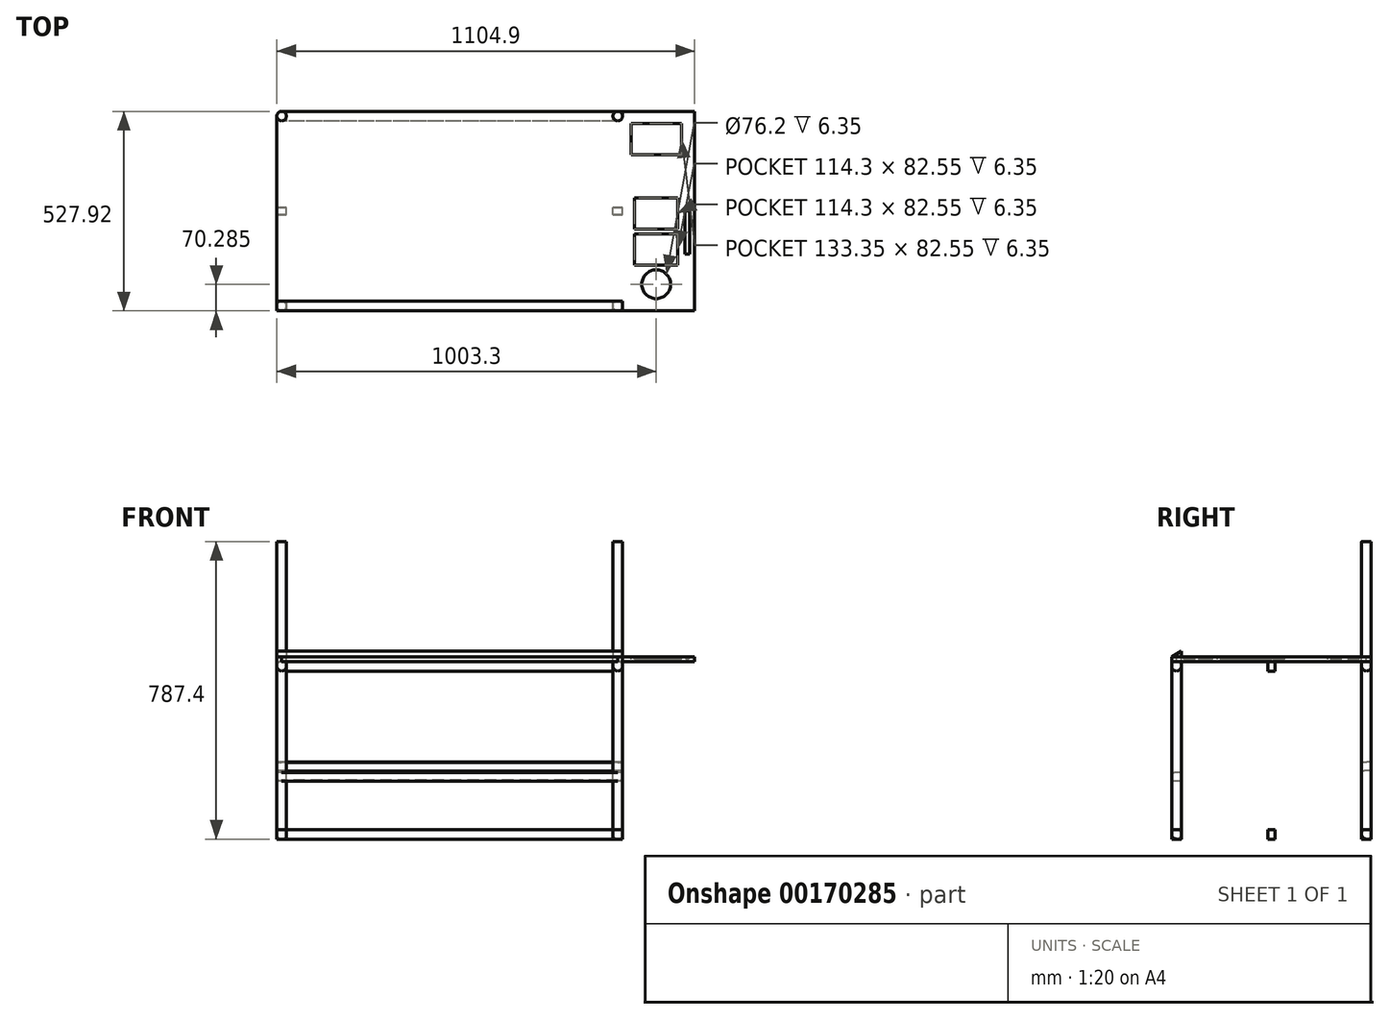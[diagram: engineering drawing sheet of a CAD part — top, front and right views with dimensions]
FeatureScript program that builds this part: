
annotation { "Feature Type Name" : "Feature", "Feature Type Description" : "" }
export const myFeature = defineFeature(function(context is Context, id is Id, definition is map)
    precondition{}
    {
        {
            var Q0;
            Q0=qCreatedBy(makeId("Top.planeOp"),FACE);
            var sketch = newSketch(context, id + "F0", { "sketchPlane" : qUnion([Q0])});
            skLineSegment(sketch, "E0.bottom", {"start": v(444.5, 251.26) * mm, "end": v(-444.5, 251.26) * mm});
            skLineSegment(sketch, "E0.top", {"start": v(444.5, -251.26) * mm, "end": v(-444.5, -251.26) * mm});
            skLineSegment(sketch, "E0.left", {"start": v(444.5, 251.26) * mm, "end": v(444.5, -251.26) * mm});
            skLineSegment(sketch, "E0.right", {"start": v(-444.5, 251.26) * mm, "end": v(-444.5, -251.26) * mm});
            skPoint(sketch, "E0.middle", {"position": v(0, 0) * mm});
            skCircle(sketch, "E1", {"center": v(-444.5, 251.26) * mm, "radius": 12.7 * mm});
            skCircle(sketch, "E2", {"center": v(-444.5, -251.26) * mm, "radius": 12.7 * mm});
            skCircle(sketch, "E3", {"center": v(444.5, -251.26) * mm, "radius": 12.7 * mm});
            skCircle(sketch, "E4", {"center": v(444.5, 251.26) * mm, "radius": 12.7 * mm});
            skLineSegment(sketch, "E5.bottom", {"start": v(-457.2, 263.96) * mm, "end": v(457.2, 263.96) * mm});
            skLineSegment(sketch, "E5.top", {"start": v(-457.2, -263.96) * mm, "end": v(457.2, -263.96) * mm});
            skLineSegment(sketch, "E5.left", {"start": v(-457.2, 263.96) * mm, "end": v(-457.2, -263.96) * mm});
            skLineSegment(sketch, "E5.right", {"start": v(457.2, 263.96) * mm, "end": v(457.2, -263.96) * mm});
            skLineSegment(sketch, "E6", {"start": v(457.2, 0) * mm, "end": v(647.7, 0) * mm});
            skPoint(sketch, "E6.endSnap0", {"position": v(457.2, 0) * mm});
            skLineSegment(sketch, "E7", {"start": v(647.7, 0) * mm, "end": v(647.7, 263.96) * mm});
            skLineSegment(sketch, "E8.bottom", {"start": v(647.7, 263.96) * mm, "end": v(457.2, 263.96) * mm});
            skLineSegment(sketch, "E8.top", {"start": v(647.7, -263.96) * mm, "end": v(457.2, -263.96) * mm});
            skPoint(sketch, "E9.centerSnap0", {"position": v(647.7, 131.98) * mm});
            skPoint(sketch, "E9.centerSnap1", {"position": v(552.45, 263.96) * mm});
            skLineSegment(sketch, "E10", {"start": v(647.7, 0) * mm, "end": v(647.7, -263.96) * mm});
            skSolve(sketch);
        }
        {
            var Q0;
            {var subQ0=sQuery(id+"F0.wireOp",EDGE,"E0.right");var subQ1=sQuery(id+"F0.wireOp",EDGE,"E0.bottom");var subQ2=makeQuery(id+"F0.imprint","INTERSECT",VERTEX,{"derivedFrom":[subQ1,subQ0]});Q0=makeQuery(id+"F0.imprint","IMPRINT",FACE,{"disambiguationData":[TD([[makeQuery(id+"F0.imprint","IMPRINT",EDGE,{"disambiguationData":[TD([[subQ2,1.0]])],"derivedFrom":subQ1}),-1.0]])]});}
            var Q1;
            {var subQ0=sQuery(id+"F0.wireOp",EDGE,"E0.right");var subQ1=sQuery(id+"F0.wireOp",EDGE,"E0.bottom");var subQ2=makeQuery(id+"F0.imprint","INTERSECT",VERTEX,{"derivedFrom":[subQ1,subQ0]});Q1=makeQuery(id+"F0.imprint","IMPRINT",FACE,{"disambiguationData":[TD([[makeQuery(id+"F0.imprint","IMPRINT",EDGE,{"disambiguationData":[TD([[subQ2,1.0]])],"derivedFrom":subQ1}),1.0]])]});}
            var Q2;
            {var subQ0=sQuery(id+"F0.wireOp",EDGE,"E0.left");var subQ1=sQuery(id+"F0.wireOp",EDGE,"E0.bottom");var subQ2=makeQuery(id+"F0.imprint","INTERSECT",VERTEX,{"derivedFrom":[subQ1,subQ0]});Q2=makeQuery(id+"F0.imprint","IMPRINT",FACE,{"disambiguationData":[TD([[makeQuery(id+"F0.imprint","IMPRINT",EDGE,{"disambiguationData":[TD([[subQ2,-1.0]])],"derivedFrom":subQ1}),-1.0]])]});}
            var Q3;
            {var subQ0=sQuery(id+"F0.wireOp",EDGE,"E0.left");var subQ1=sQuery(id+"F0.wireOp",EDGE,"E0.bottom");var subQ2=makeQuery(id+"F0.imprint","INTERSECT",VERTEX,{"derivedFrom":[subQ1,subQ0]});Q3=makeQuery(id+"F0.imprint","IMPRINT",FACE,{"disambiguationData":[TD([[makeQuery(id+"F0.imprint","IMPRINT",EDGE,{"disambiguationData":[TD([[subQ2,-1.0]])],"derivedFrom":subQ1}),1.0]])]});}
            extrude(context, id + "F1", {"entities" : qUnion([Q0, Q1, Q2, Q3]), "depth" : 304.8 * mm});
        }
        {
            var Q0;
            {var subQ0=sQuery(id+"F0.wireOp",EDGE,"E0.right");var subQ1=sQuery(id+"F0.wireOp",EDGE,"E0.top");var subQ2=makeQuery(id+"F0.imprint","INTERSECT",VERTEX,{"derivedFrom":[subQ1,subQ0]});Q0=makeQuery(id+"F0.imprint","IMPRINT",FACE,{"disambiguationData":[TD([[makeQuery(id+"F0.imprint","IMPRINT",EDGE,{"disambiguationData":[TD([[subQ2,1.0]])],"derivedFrom":subQ1}),1.0]])]});}
            var Q1;
            {var subQ0=sQuery(id+"F0.wireOp",EDGE,"E0.right");var subQ1=sQuery(id+"F0.wireOp",EDGE,"E0.top");var subQ2=makeQuery(id+"F0.imprint","INTERSECT",VERTEX,{"derivedFrom":[subQ1,subQ0]});Q1=makeQuery(id+"F0.imprint","IMPRINT",FACE,{"disambiguationData":[TD([[makeQuery(id+"F0.imprint","IMPRINT",EDGE,{"disambiguationData":[TD([[subQ2,1.0]])],"derivedFrom":subQ1}),-1.0]])]});}
            var Q2;
            {var subQ0=sQuery(id+"F0.wireOp",EDGE,"E0.left");var subQ1=sQuery(id+"F0.wireOp",EDGE,"E0.top");var subQ2=makeQuery(id+"F0.imprint","INTERSECT",VERTEX,{"derivedFrom":[subQ1,subQ0]});Q2=makeQuery(id+"F0.imprint","IMPRINT",FACE,{"disambiguationData":[TD([[makeQuery(id+"F0.imprint","IMPRINT",EDGE,{"disambiguationData":[TD([[subQ2,-1.0]])],"derivedFrom":subQ1}),-1.0]])]});}
            var Q3;
            {var subQ0=sQuery(id+"F0.wireOp",EDGE,"E0.left");var subQ1=sQuery(id+"F0.wireOp",EDGE,"E0.top");var subQ2=makeQuery(id+"F0.imprint","INTERSECT",VERTEX,{"derivedFrom":[subQ1,subQ0]});Q3=makeQuery(id+"F0.imprint","IMPRINT",FACE,{"disambiguationData":[TD([[makeQuery(id+"F0.imprint","IMPRINT",EDGE,{"disambiguationData":[TD([[subQ2,-1.0]])],"derivedFrom":subQ1}),1.0]])]});}
            extrude(context, id + "F2", {"entities" : qUnion([Q0, Q1, Q2, Q3]), "oppositeDirection" : true, "depth" : 457.2 * mm});
        }
        {
            var Q0;
            {var subQ0=sQuery(id+"F0.wireOp",EDGE,"E0.left");var subQ1=sQuery(id+"F0.wireOp",EDGE,"E0.bottom");var subQ2=makeQuery(id+"F0.imprint","INTERSECT",VERTEX,{"derivedFrom":[subQ1,subQ0]});Q0=makeQuery(id+"F0.imprint","IMPRINT",FACE,{"disambiguationData":[TD([[makeQuery(id+"F0.imprint","IMPRINT",EDGE,{"disambiguationData":[TD([[subQ2,-1.0]])],"derivedFrom":subQ1}),1.0]])]});}
            var Q1;
            {var subQ0=sQuery(id+"F0.wireOp",EDGE,"E0.left");var subQ1=sQuery(id+"F0.wireOp",EDGE,"E0.bottom");var subQ2=makeQuery(id+"F0.imprint","INTERSECT",VERTEX,{"derivedFrom":[subQ1,subQ0]});Q1=makeQuery(id+"F0.imprint","IMPRINT",FACE,{"disambiguationData":[TD([[makeQuery(id+"F0.imprint","IMPRINT",EDGE,{"disambiguationData":[TD([[subQ2,-1.0]])],"derivedFrom":subQ1}),-1.0]])]});}
            var Q2;
            {var subQ0=sQuery(id+"F0.wireOp",EDGE,"E0.right");var subQ1=sQuery(id+"F0.wireOp",EDGE,"E0.bottom");var subQ2=makeQuery(id+"F0.imprint","INTERSECT",VERTEX,{"derivedFrom":[subQ1,subQ0]});Q2=makeQuery(id+"F0.imprint","IMPRINT",FACE,{"disambiguationData":[TD([[makeQuery(id+"F0.imprint","IMPRINT",EDGE,{"disambiguationData":[TD([[subQ2,1.0]])],"derivedFrom":subQ1}),1.0]])]});}
            var Q3;
            {var subQ0=sQuery(id+"F0.wireOp",EDGE,"E0.right");var subQ1=sQuery(id+"F0.wireOp",EDGE,"E0.bottom");var subQ2=makeQuery(id+"F0.imprint","INTERSECT",VERTEX,{"derivedFrom":[subQ1,subQ0]});Q3=makeQuery(id+"F0.imprint","IMPRINT",FACE,{"disambiguationData":[TD([[makeQuery(id+"F0.imprint","IMPRINT",EDGE,{"disambiguationData":[TD([[subQ2,1.0]])],"derivedFrom":subQ1}),-1.0]])]});}
            extrude(context, id + "F3", {"entities" : qUnion([Q0, Q1, Q2, Q3]), "oppositeDirection" : true, "depth" : 457.2 * mm});
        }
        {
            var Q0;
            {var subQ0=sQuery(id+"F0.wireOp",EDGE,"E1");var subQ1=sQuery(id+"F0.wireOp",EDGE,"E0.right");var subQ2=makeQuery(id+"F0.imprint","INTERSECT",VERTEX,{"derivedFrom":[subQ1,subQ0]});Q0=makeQuery(id+"F0.imprint","IMPRINT",FACE,{"disambiguationData":[TD([[makeQuery(id+"F0.imprint","IMPRINT",EDGE,{"disambiguationData":[TD([[subQ2,-1.0]])],"derivedFrom":subQ1}),-1.0]])]});}
            var Q1;
            {var subQ0=sQuery(id+"F0.wireOp",EDGE,"E3");var subQ1=sQuery(id+"F0.wireOp",EDGE,"E0.top");var subQ2=makeQuery(id+"F0.imprint","INTERSECT",VERTEX,{"derivedFrom":[subQ1,subQ0]});Q1=makeQuery(id+"F0.imprint","IMPRINT",FACE,{"disambiguationData":[TD([[makeQuery(id+"F0.imprint","IMPRINT",EDGE,{"disambiguationData":[TD([[subQ2,-1.0]])],"derivedFrom":subQ1}),1.0]])]});}
            var Q2;
            {var subQ0=sQuery(id+"F0.wireOp",EDGE,"E4");var subQ1=sQuery(id+"F0.wireOp",EDGE,"E0.left");var subQ2=makeQuery(id+"F0.imprint","INTERSECT",VERTEX,{"derivedFrom":[subQ1,subQ0]});Q2=makeQuery(id+"F0.imprint","IMPRINT",FACE,{"disambiguationData":[TD([[makeQuery(id+"F0.imprint","IMPRINT",EDGE,{"disambiguationData":[TD([[subQ2,-1.0]])],"derivedFrom":subQ1}),1.0]])]});}
            var Q3;
            {var subQ0=sQuery(id+"F0.wireOp",EDGE,"E4");var subQ1=sQuery(id+"F0.wireOp",EDGE,"E0.bottom");var subQ2=makeQuery(id+"F0.imprint","INTERSECT",VERTEX,{"derivedFrom":[subQ1,subQ0]});Q3=makeQuery(id+"F0.imprint","IMPRINT",FACE,{"disambiguationData":[TD([[makeQuery(id+"F0.imprint","IMPRINT",EDGE,{"disambiguationData":[TD([[subQ2,-1.0]])],"derivedFrom":subQ1}),-1.0]])]});}
            var Q4;
            {var subQ5=sQuery(id+"F0.wireOp",EDGE,"E4");var subQ13=sQuery(id+"F0.wireOp",EDGE,"E0.bottom");var subQ14=makeQuery(id+"F0.imprint","INTERSECT",VERTEX,{"derivedFrom":[subQ13,subQ5]});Q4=makeQuery(id+"F0.imprint","IMPRINT",FACE,{"disambiguationData":[TD([[makeQuery(id+"F0.imprint","IMPRINT",EDGE,{"disambiguationData":[TD([[subQ14,-1.0]])],"derivedFrom":subQ13}),1.0]])]});}
            var Q5;
            {var subQ0=sQuery(id+"F0.wireOp",EDGE,"E6");Q5=makeQuery(id+"F0.imprint","IMPRINT",FACE,{"disambiguationData":[TD([[makeQuery(id+"F0.imprint","IMPRINT",EDGE,{"derivedFrom":subQ0}),1.0]])]});}
            var Q6;
            {var subQ0=sQuery(id+"F0.wireOp",EDGE,"E6");Q6=makeQuery(id+"F0.imprint","IMPRINT",FACE,{"disambiguationData":[TD([[makeQuery(id+"F0.imprint","IMPRINT",EDGE,{"derivedFrom":subQ0}),-1.0]])]});}
            extrude(context, id + "F4", {"entities" : qUnion([Q0, Q1, Q2, Q3, Q4, Q5, Q6]), "oppositeDirection" : true, "depth" : 12.7 * mm});
        }
        {
            var Q0;
            Q0=qCreatedBy(makeId("Top.planeOp"),FACE);
            cPlane(context, id + "F5", {"entities" : qUnion([Q0]), "cplaneType" : CPlaneType.OFFSET, "offset" : 457.2 * mm, "oppositeDirection" : true, "width" : 152.4 * mm, "height" : 152.4 * mm});
        }
        {
            var Q0;
            Q0=qCreatedBy(id+"F5.planeOp",FACE);
            var sketch = newSketch(context, id + "F6", { "sketchPlane" : qUnion([Q0])});
            skLineSegment(sketch, "E11.bottom", {"start": v(-457.2, 263.96) * mm, "end": v(457.2, 263.96) * mm});
            skLineSegment(sketch, "E11.top", {"start": v(-457.2, -263.96) * mm, "end": v(457.2, -263.96) * mm});
            skLineSegment(sketch, "E11.left", {"start": v(-457.2, 263.96) * mm, "end": v(-457.2, -263.96) * mm});
            skLineSegment(sketch, "E11.right", {"start": v(457.2, 263.96) * mm, "end": v(457.2, -263.96) * mm});
            skPoint(sketch, "E11.middle", {"position": v(0, 0) * mm});
            skLineSegment(sketch, "E12", {"start": v(-457.2, 263.96) * mm, "end": v(-444.5, 263.96) * mm});
            skLineSegment(sketch, "E13", {"start": v(-444.5, 263.96) * mm, "end": v(-444.5, 251.26) * mm});
            skLineSegment(sketch, "E14", {"start": v(457.2, -263.96) * mm, "end": v(457.2, -251.26) * mm});
            skLineSegment(sketch, "E15", {"start": v(457.2, -251.26) * mm, "end": v(444.5, -251.26) * mm});
            skLineSegment(sketch, "E16.bottom", {"start": v(-444.5, 251.26) * mm, "end": v(444.5, 251.26) * mm});
            skLineSegment(sketch, "E16.top", {"start": v(-444.5, -251.26) * mm, "end": v(444.5, -251.26) * mm});
            skLineSegment(sketch, "E16.left", {"start": v(-444.5, 251.26) * mm, "end": v(-444.5, -251.26) * mm});
            skLineSegment(sketch, "E16.right", {"start": v(444.5, 251.26) * mm, "end": v(444.5, -251.26) * mm});
            skCircle(sketch, "E17", {"center": v(-444.5, 251.26) * mm, "radius": 12.7 * mm});
            skCircle(sketch, "E18", {"center": v(-444.5, -251.26) * mm, "radius": 12.7 * mm});
            skCircle(sketch, "E19", {"center": v(444.5, -251.26) * mm, "radius": 12.7 * mm});
            skCircle(sketch, "E20", {"center": v(444.5, 251.26) * mm, "radius": 12.7 * mm});
            skSolve(sketch);
        }
        {
            var Q0;
            {var subQ3=sQuery(id+"F6.wireOp",EDGE,"E16.left");var subQ4=sQuery(id+"F6.wireOp",EDGE,"E16.top");var subQ5=makeQuery(id+"F6.imprint","INTERSECT",VERTEX,{"derivedFrom":[subQ4,subQ3]});Q0=makeQuery(id+"F6.imprint","IMPRINT",FACE,{"disambiguationData":[TD([[makeQuery(id+"F6.imprint","IMPRINT",EDGE,{"disambiguationData":[TD([[subQ5,-1.0]])],"derivedFrom":subQ4}),-1.0]])]});}
            var Q1;
            {var subQ0=sQuery(id+"F6.wireOp",EDGE,"E16.left");var subQ1=sQuery(id+"F6.wireOp",EDGE,"E16.top");var subQ2=makeQuery(id+"F6.imprint","INTERSECT",VERTEX,{"derivedFrom":[subQ1,subQ0]});Q1=makeQuery(id+"F6.imprint","IMPRINT",FACE,{"disambiguationData":[TD([[makeQuery(id+"F6.imprint","IMPRINT",EDGE,{"disambiguationData":[TD([[subQ2,-1.0]])],"derivedFrom":subQ1}),1.0]])]});}
            var Q2;
            {var subQ0=sQuery(id+"F6.wireOp",EDGE,"E15");Q2=makeQuery(id+"F6.imprint","IMPRINT",FACE,{"disambiguationData":[TD([[makeQuery(id+"F6.imprint","IMPRINT",EDGE,{"derivedFrom":subQ0}),-1.0]])]});}
            var Q3;
            {var subQ1=sQuery(id+"F6.wireOp",EDGE,"E16.top");var subQ3=sQuery(id+"F6.wireOp",EDGE,"E19");var subQ4=makeQuery(id+"F6.imprint","INTERSECT",VERTEX,{"derivedFrom":[subQ1,subQ3]});Q3=makeQuery(id+"F6.imprint","IMPRINT",FACE,{"disambiguationData":[TD([[makeQuery(id+"F6.imprint","IMPRINT",EDGE,{"disambiguationData":[TD([[subQ4,1.0]])],"derivedFrom":subQ3}),1.0]])]});}
            var Q4;
            {var subQ0=sQuery(id+"F6.wireOp",EDGE,"E15");Q4=makeQuery(id+"F6.imprint","IMPRINT",FACE,{"disambiguationData":[TD([[makeQuery(id+"F6.imprint","IMPRINT",EDGE,{"derivedFrom":subQ0}),1.0]])]});}
            var Q5;
            {var subQ0=sQuery(id+"F6.wireOp",EDGE,"E16.right");var subQ1=sQuery(id+"F6.wireOp",EDGE,"E16.bottom");var subQ2=makeQuery(id+"F6.imprint","INTERSECT",VERTEX,{"derivedFrom":[subQ1,subQ0]});Q5=makeQuery(id+"F6.imprint","IMPRINT",FACE,{"disambiguationData":[TD([[makeQuery(id+"F6.imprint","IMPRINT",EDGE,{"disambiguationData":[TD([[subQ2,1.0]])],"derivedFrom":subQ1}),-1.0]])]});}
            var Q6;
            {var subQ2=sQuery(id+"F6.wireOp",EDGE,"E16.bottom");var subQ5=sQuery(id+"F6.wireOp",EDGE,"E16.right");var subQ7=makeQuery(id+"F6.imprint","INTERSECT",VERTEX,{"derivedFrom":[subQ2,subQ5]});Q6=makeQuery(id+"F6.imprint","IMPRINT",FACE,{"disambiguationData":[TD([[makeQuery(id+"F6.imprint","IMPRINT",EDGE,{"disambiguationData":[TD([[subQ7,1.0]])],"derivedFrom":subQ2}),1.0]])]});}
            var Q7;
            {var subQ1=sQuery(id+"F6.wireOp",EDGE,"E16.bottom");var subQ3=sQuery(id+"F6.wireOp",EDGE,"E17");var subQ4=makeQuery(id+"F6.imprint","INTERSECT",VERTEX,{"derivedFrom":[subQ1,subQ3]});Q7=makeQuery(id+"F6.imprint","IMPRINT",FACE,{"disambiguationData":[TD([[makeQuery(id+"F6.imprint","IMPRINT",EDGE,{"disambiguationData":[TD([[subQ4,1.0]])],"derivedFrom":subQ3}),1.0]])]});}
            var Q8;
            {var subQ0=sQuery(id+"F6.wireOp",EDGE,"E13");Q8=makeQuery(id+"F6.imprint","IMPRINT",FACE,{"disambiguationData":[TD([[makeQuery(id+"F6.imprint","IMPRINT",EDGE,{"derivedFrom":subQ0}),1.0]])]});}
            var Q9;
            {var subQ0=sQuery(id+"F6.wireOp",EDGE,"E13");Q9=makeQuery(id+"F6.imprint","IMPRINT",FACE,{"disambiguationData":[TD([[makeQuery(id+"F6.imprint","IMPRINT",EDGE,{"derivedFrom":subQ0}),-1.0]])]});}
            extrude(context, id + "F7", {"entities" : qUnion([Q0, Q1, Q2, Q3, Q4, Q5, Q6, Q7, Q8, Q9]), "oppositeDirection" : true, "depth" : 25.4 * mm});
        }
        {
            var Q0;
            Q0=qCreatedBy(makeId("Right.planeOp"),FACE);
            var sketch = newSketch(context, id + "F8", { "sketchPlane" : qUnion([Q0])});
            skLineSegment(sketch, "E21.bottom", {"start": v(-251.26, -25.4) * mm, "end": v(251.26, -25.4) * mm});
            skLineSegment(sketch, "E21.top", {"start": v(-251.26, 25.4) * mm, "end": v(251.26, 25.4) * mm});
            skLineSegment(sketch, "E21.left", {"start": v(-251.26, -25.4) * mm, "end": v(-251.26, 25.4) * mm});
            skLineSegment(sketch, "E21.right", {"start": v(251.26, -25.4) * mm, "end": v(251.26, 25.4) * mm});
            skPoint(sketch, "E21.middle", {"position": v(0, 0) * mm});
            skLineSegment(sketch, "E22", {"start": v(0, 0) * mm, "end": v(0, -469.9) * mm});
            skLineSegment(sketch, "E23.bottom", {"start": v(251.26, -469.9) * mm, "end": v(-251.26, -469.9) * mm});
            skLineSegment(sketch, "E23.top", {"start": v(251.26, -469.9) * mm, "end": v(-251.26, -469.9) * mm});
            skLineSegment(sketch, "E23.left", {"start": v(251.26, -469.9) * mm, "end": v(251.26, -469.9) * mm});
            skLineSegment(sketch, "E23.right", {"start": v(-251.26, -469.9) * mm, "end": v(-251.26, -469.9) * mm});
            skPoint(sketch, "E23.middle", {"position": v(0, -469.9) * mm});
            skCircle(sketch, "E24", {"center": v(-251.26, -25.4) * mm, "radius": 12.7 * mm});
            skCircle(sketch, "E25", {"center": v(251.26, -25.4) * mm, "radius": 12.7 * mm});
            skCircle(sketch, "E26", {"center": v(251.26, -469.9) * mm, "radius": 12.7 * mm});
            skCircle(sketch, "E27", {"center": v(-251.26, -469.9) * mm, "radius": 12.7 * mm});
            skSolve(sketch);
        }
        {
            var Q0;
            {var subQ0=sQuery(id+"F8.wireOp",EDGE,"E21.left");var subQ1=sQuery(id+"F8.wireOp",EDGE,"E21.bottom");var subQ2=makeQuery(id+"F8.imprint","INTERSECT",VERTEX,{"derivedFrom":[subQ1,subQ0]});Q0=makeQuery(id+"F8.imprint","IMPRINT",FACE,{"disambiguationData":[TD([[makeQuery(id+"F8.imprint","IMPRINT",EDGE,{"disambiguationData":[TD([[subQ2,-1.0]])],"derivedFrom":subQ1}),-1.0]])]});}
            var Q1;
            {var subQ0=sQuery(id+"F8.wireOp",EDGE,"E21.left");var subQ1=sQuery(id+"F8.wireOp",EDGE,"E21.bottom");var subQ2=makeQuery(id+"F8.imprint","INTERSECT",VERTEX,{"derivedFrom":[subQ1,subQ0]});Q1=makeQuery(id+"F8.imprint","IMPRINT",FACE,{"disambiguationData":[TD([[makeQuery(id+"F8.imprint","IMPRINT",EDGE,{"disambiguationData":[TD([[subQ2,-1.0]])],"derivedFrom":subQ1}),1.0]])]});}
            var Q2;
            {var subQ0=sQuery(id+"F8.wireOp",EDGE,"E21.right");var subQ1=sQuery(id+"F8.wireOp",EDGE,"E21.bottom");var subQ2=makeQuery(id+"F8.imprint","INTERSECT",VERTEX,{"derivedFrom":[subQ1,subQ0]});Q2=makeQuery(id+"F8.imprint","IMPRINT",FACE,{"disambiguationData":[TD([[makeQuery(id+"F8.imprint","IMPRINT",EDGE,{"disambiguationData":[TD([[subQ2,1.0]])],"derivedFrom":subQ1}),-1.0]])]});}
            var Q3;
            {var subQ0=sQuery(id+"F8.wireOp",EDGE,"E21.right");var subQ1=sQuery(id+"F8.wireOp",EDGE,"E21.bottom");var subQ2=makeQuery(id+"F8.imprint","INTERSECT",VERTEX,{"derivedFrom":[subQ1,subQ0]});Q3=makeQuery(id+"F8.imprint","IMPRINT",FACE,{"disambiguationData":[TD([[makeQuery(id+"F8.imprint","IMPRINT",EDGE,{"disambiguationData":[TD([[subQ2,1.0]])],"derivedFrom":subQ1}),1.0]])]});}
            var Q4;
            Q4=makeQuery(id+"F8.imprint","IMPRINT",FACE,{"disambiguationData":[TD([[makeQuery(id+"F8.imprint","IMPRINT",EDGE,{"derivedFrom":sQuery(id+"F8.wireOp",EDGE,"E26")}),1.0]])]});
            var Q5;
            Q5=makeQuery(id+"F8.imprint","IMPRINT",FACE,{"disambiguationData":[TD([[makeQuery(id+"F8.imprint","IMPRINT",EDGE,{"derivedFrom":sQuery(id+"F8.wireOp",EDGE,"E27")}),1.0]])]});
            extrude(context, id + "F9", {"entities" : qUnion([Q0, Q1, Q2, Q3, Q4, Q5]), "endBound" : BoundingType.SYMMETRIC, "depth" : 863.6 * mm});
        }
        {
            var Q0;
            Q0=qCreatedBy(makeId("Front.planeOp"),FACE);
            var sketch = newSketch(context, id + "F10", { "sketchPlane" : qUnion([Q0])});
            skLineSegment(sketch, "E28.bottom", {"start": v(444.5, 25.4) * mm, "end": v(-444.5, 25.4) * mm});
            skLineSegment(sketch, "E28.top", {"start": v(444.5, -25.4) * mm, "end": v(-444.5, -25.4) * mm});
            skLineSegment(sketch, "E28.left", {"start": v(444.5, 25.4) * mm, "end": v(444.5, -25.4) * mm});
            skLineSegment(sketch, "E28.right", {"start": v(-444.5, 25.4) * mm, "end": v(-444.5, -25.4) * mm});
            skPoint(sketch, "E28.middle", {"position": v(0, 0) * mm});
            skLineSegment(sketch, "E29", {"start": v(0, 0) * mm, "end": v(0, -469.9) * mm});
            skLineSegment(sketch, "E30.bottom", {"start": v(444.5, -469.9) * mm, "end": v(-444.5, -469.9) * mm});
            skLineSegment(sketch, "E30.top", {"start": v(444.5, -469.9) * mm, "end": v(-444.5, -469.9) * mm});
            skLineSegment(sketch, "E30.left", {"start": v(444.5, -469.9) * mm, "end": v(444.5, -469.9) * mm});
            skLineSegment(sketch, "E30.right", {"start": v(-444.5, -469.9) * mm, "end": v(-444.5, -469.9) * mm});
            skPoint(sketch, "E30.middle", {"position": v(0, -469.9) * mm});
            skCircle(sketch, "E31", {"center": v(-444.5, -25.4) * mm, "radius": 12.7 * mm});
            skCircle(sketch, "E32", {"center": v(444.5, -25.4) * mm, "radius": 12.7 * mm});
            skCircle(sketch, "E33", {"center": v(444.5, -469.9) * mm, "radius": 12.7 * mm});
            skCircle(sketch, "E34", {"center": v(-444.5, -469.9) * mm, "radius": 12.7 * mm});
            skSolve(sketch);
        }
        {
            var Q0;
            {var subQ0=sQuery(id+"F10.wireOp",EDGE,"E28.right");var subQ1=sQuery(id+"F10.wireOp",EDGE,"E28.top");var subQ2=makeQuery(id+"F10.imprint","INTERSECT",VERTEX,{"derivedFrom":[subQ1,subQ0]});Q0=makeQuery(id+"F10.imprint","IMPRINT",FACE,{"disambiguationData":[TD([[makeQuery(id+"F10.imprint","IMPRINT",EDGE,{"disambiguationData":[TD([[subQ2,1.0]])],"derivedFrom":subQ1}),1.0]])]});}
            var Q1;
            {var subQ0=sQuery(id+"F10.wireOp",EDGE,"E28.right");var subQ1=sQuery(id+"F10.wireOp",EDGE,"E28.top");var subQ2=makeQuery(id+"F10.imprint","INTERSECT",VERTEX,{"derivedFrom":[subQ1,subQ0]});Q1=makeQuery(id+"F10.imprint","IMPRINT",FACE,{"disambiguationData":[TD([[makeQuery(id+"F10.imprint","IMPRINT",EDGE,{"disambiguationData":[TD([[subQ2,1.0]])],"derivedFrom":subQ1}),-1.0]])]});}
            var Q2;
            {var subQ0=sQuery(id+"F10.wireOp",EDGE,"E28.left");var subQ1=sQuery(id+"F10.wireOp",EDGE,"E28.top");var subQ2=makeQuery(id+"F10.imprint","INTERSECT",VERTEX,{"derivedFrom":[subQ1,subQ0]});Q2=makeQuery(id+"F10.imprint","IMPRINT",FACE,{"disambiguationData":[TD([[makeQuery(id+"F10.imprint","IMPRINT",EDGE,{"disambiguationData":[TD([[subQ2,-1.0]])],"derivedFrom":subQ1}),1.0]])]});}
            var Q3;
            {var subQ0=sQuery(id+"F10.wireOp",EDGE,"E28.left");var subQ1=sQuery(id+"F10.wireOp",EDGE,"E28.top");var subQ2=makeQuery(id+"F10.imprint","INTERSECT",VERTEX,{"derivedFrom":[subQ1,subQ0]});Q3=makeQuery(id+"F10.imprint","IMPRINT",FACE,{"disambiguationData":[TD([[makeQuery(id+"F10.imprint","IMPRINT",EDGE,{"disambiguationData":[TD([[subQ2,-1.0]])],"derivedFrom":subQ1}),-1.0]])]});}
            var Q4;
            Q4=makeQuery(id+"F10.imprint","IMPRINT",FACE,{"disambiguationData":[TD([[makeQuery(id+"F10.imprint","IMPRINT",EDGE,{"derivedFrom":sQuery(id+"F10.wireOp",EDGE,"E34")}),1.0]])]});
            var Q5;
            Q5=makeQuery(id+"F10.imprint","IMPRINT",FACE,{"disambiguationData":[TD([[makeQuery(id+"F10.imprint","IMPRINT",EDGE,{"derivedFrom":sQuery(id+"F10.wireOp",EDGE,"E33")}),1.0]])]});
            extrude(context, id + "F11", {"entities" : qUnion([Q0, Q1, Q2, Q3, Q4, Q5]), "endBound" : BoundingType.SYMMETRIC, "depth" : ((12 * sqrt(3)) - 2) * mm});
        }
        {
            var Q0;
            Q0=qCreatedBy(makeId("Right.planeOp"),FACE);
            cPlane(context, id + "F12", {"entities" : qUnion([Q0]), "cplaneType" : CPlaneType.OFFSET, "offset" : 457.2 * mm, "width" : 152.4 * mm, "height" : 152.4 * mm});
        }
        {
            var Q0;
            Q0=qCreatedBy(id+"F12.planeOp",FACE);
            var sketch = newSketch(context, id + "F13", { "sketchPlane" : qUnion([Q0])});
            skLineSegment(sketch, "E35", {"start": v(0, 0) * mm, "end": v(-263.96, 0) * mm});
            skLineSegment(sketch, "E36", {"start": v(-238.56, 0) * mm, "end": v(-238.56, 14.66) * mm});
            skLineSegment(sketch, "E37", {"start": v(-263.96, 0) * mm, "end": v(-238.56, 14.66) * mm});
            skSolve(sketch);
        }
        {
            var Q0;
            {var subQ2=sQuery(id+"F13.wireOp",EDGE,"E36");Q0=makeQuery(id+"F13.imprint","IMPRINT",FACE,{"disambiguationData":[TD([[makeQuery(id+"F13.imprint","IMPRINT",EDGE,{"derivedFrom":subQ2}),1.0]])]});}
            extrude(context, id + "F14", {"entities" : qUnion([Q0]), "oppositeDirection" : true, "depth" : 914.4 * mm});
        }
        {
            var Q0;
            Q0=makeQuery(id+"F4.opExtrude","CAP_FACE",FACE,{"disambiguationData":[OSD([sQuery(id+"F0.wireOp",EDGE,"E1"),sQuery(id+"F0.wireOp",EDGE,"E2"),sQuery(id+"F0.wireOp",EDGE,"E3"),sQuery(id+"F0.wireOp",EDGE,"E4"),sQuery(id+"F0.wireOp",EDGE,"E5.bottom"),sQuery(id+"F0.wireOp",EDGE,"E5.top"),sQuery(id+"F0.wireOp",EDGE,"E5.left"),sQuery(id+"F0.wireOp",EDGE,"E5.right"),sQuery(id+"F0.wireOp",EDGE,"E7"),sQuery(id+"F0.wireOp",EDGE,"E8.bottom"),sQuery(id+"F0.wireOp",EDGE,"E8.top"),sQuery(id+"F0.wireOp",EDGE,"E10")])],"isStart":true});
            var sketch = newSketch(context, id + "F15", { "sketchPlane" : qUnion([Q0])});
            skLineSegment(sketch, "E38", {"start": v(0, 0) * mm, "end": v(546.1, 0) * mm});
            skLineSegment(sketch, "E39", {"start": v(546.1, 0) * mm, "end": v(546.1, 190.5) * mm});
            skLineSegment(sketch, "E40.bottom", {"start": v(612.78, 231.77) * mm, "end": v(479.43, 231.77) * mm});
            skLineSegment(sketch, "E40.top", {"start": v(612.78, 149.22) * mm, "end": v(479.43, 149.22) * mm});
            skLineSegment(sketch, "E40.left", {"start": v(612.78, 231.77) * mm, "end": v(612.78, 149.22) * mm});
            skLineSegment(sketch, "E40.right", {"start": v(479.43, 231.77) * mm, "end": v(479.43, 149.22) * mm});
            skPoint(sketch, "E40.middle", {"position": v(546.1, 190.5) * mm});
            skLineSegment(sketch, "E41", {"start": v(546.1, 0) * mm, "end": v(546.1, 130.17) * mm});
            skLineSegment(sketch, "E42.bottom", {"start": v(479.43, 130.18) * mm, "end": v(612.78, 130.17) * mm});
            skLineSegment(sketch, "E42.top", {"start": v(479.43, 47.63) * mm, "end": v(612.78, 47.62) * mm});
            skLineSegment(sketch, "E42.left", {"start": v(479.43, 130.17) * mm, "end": v(479.43, 47.63) * mm});
            skLineSegment(sketch, "E42.right", {"start": v(612.78, 130.17) * mm, "end": v(612.78, 47.63) * mm});
            skLineSegment(sketch, "E43", {"start": v(546.1, 47.62) * mm, "end": v(546.1, -6.35) * mm});
            skLineSegment(sketch, "E44.bottom", {"start": v(603.25, 34.93) * mm, "end": v(488.95, 34.93) * mm});
            skLineSegment(sketch, "E44.top", {"start": v(603.25, -47.62) * mm, "end": v(488.95, -47.62) * mm});
            skLineSegment(sketch, "E44.left", {"start": v(603.25, 34.93) * mm, "end": v(603.25, -47.62) * mm});
            skLineSegment(sketch, "E44.right", {"start": v(488.95, 34.93) * mm, "end": v(488.95, -47.62) * mm});
            skPoint(sketch, "E44.middle", {"position": v(546.1, -6.35) * mm});
            skLineSegment(sketch, "E45", {"start": v(546.1, -47.62) * mm, "end": v(546.1, -60.32) * mm});
            skLineSegment(sketch, "E46.bottom", {"start": v(488.95, -60.32) * mm, "end": v(603.25, -60.32) * mm});
            skLineSegment(sketch, "E46.top", {"start": v(488.95, -142.87) * mm, "end": v(603.25, -142.87) * mm});
            skLineSegment(sketch, "E46.left", {"start": v(488.95, -60.32) * mm, "end": v(488.95, -142.87) * mm});
            skLineSegment(sketch, "E46.right", {"start": v(603.25, -60.32) * mm, "end": v(603.25, -142.87) * mm});
            skLineSegment(sketch, "E47", {"start": v(546.1, -142.87) * mm, "end": v(546.1, -193.67) * mm});
            skCircle(sketch, "E48", {"center": v(546.1, -193.67) * mm, "radius": 38.1 * mm});
            skLineSegment(sketch, "E49.bottom", {"start": v(622.3, -114.3) * mm, "end": v(635, -114.3) * mm});
            skLineSegment(sketch, "E49.top", {"start": v(622.3, 0) * mm, "end": v(635, 0) * mm});
            skLineSegment(sketch, "E49.left", {"start": v(622.3, -114.3) * mm, "end": v(622.3, 0) * mm});
            skLineSegment(sketch, "E49.right", {"start": v(635, -114.3) * mm, "end": v(635, 0) * mm});
            skLineSegment(sketch, "E50", {"start": v(628.65, -114.3) * mm, "end": v(628.65, 0) * mm});
            skLineSegment(sketch, "E51", {"start": v(622.3, 0) * mm, "end": v(603.25, 0) * mm});
            skSolve(sketch);
        }
        {
            var Q0;
            Q0=makeQuery(id+"F15.imprint","IMPRINT",FACE,{"disambiguationData":[TD([[makeQuery(id+"F15.imprint","IMPRINT",EDGE,{"derivedFrom":sQuery(id+"F15.wireOp",EDGE,"E40.bottom")}),1.0]])]});
            var Q1;
            {var subQ0=sQuery(id+"F15.wireOp",EDGE,"E41");Q1=makeQuery(id+"F15.imprint","IMPRINT",FACE,{"disambiguationData":[TD([[makeQuery(id+"F15.imprint","IMPRINT",EDGE,{"derivedFrom":subQ0}),-1.0]])]});}
            var Q2;
            {var subQ0=sQuery(id+"F15.wireOp",EDGE,"E41");Q2=makeQuery(id+"F15.imprint","IMPRINT",FACE,{"disambiguationData":[TD([[makeQuery(id+"F15.imprint","IMPRINT",EDGE,{"derivedFrom":subQ0}),1.0]])]});}
            var Q3;
            {var subQ0=sQuery(id+"F15.wireOp",EDGE,"E44.left");Q3=makeQuery(id+"F15.imprint","IMPRINT",FACE,{"disambiguationData":[TD([[makeQuery(id+"F15.imprint","IMPRINT",EDGE,{"derivedFrom":subQ0}),-1.0]])]});}
            var Q4;
            {var subQ0=sQuery(id+"F15.wireOp",EDGE,"E43");var subQ1=sQuery(id+"F15.wireOp",EDGE,"E38");var subQ2=makeQuery(id+"F15.imprint","INTERSECT",VERTEX,{"derivedFrom":[subQ1,subQ0]});Q4=makeQuery(id+"F15.imprint","IMPRINT",FACE,{"disambiguationData":[TD([[makeQuery(id+"F15.imprint","IMPRINT",EDGE,{"disambiguationData":[TD([[subQ2,1.0]])],"derivedFrom":subQ1}),1.0]])]});}
            var Q5;
            {var subQ0=sQuery(id+"F15.wireOp",EDGE,"E46.left");Q5=makeQuery(id+"F15.imprint","IMPRINT",FACE,{"disambiguationData":[TD([[makeQuery(id+"F15.imprint","IMPRINT",EDGE,{"derivedFrom":subQ0}),1.0]])]});}
            var Q6;
            Q6=makeQuery(id+"F15.imprint","IMPRINT",FACE,{"disambiguationData":[TD([[makeQuery(id+"F15.imprint","IMPRINT",EDGE,{"derivedFrom":sQuery(id+"F15.wireOp",EDGE,"E48")}),1.0]])]});
            extrude(context, id + "F16", {"entities" : qUnion([Q0, Q1, Q2, Q3, Q4, Q5, Q6]), "operationType" : NewBodyOperationType.REMOVE, "oppositeDirection" : true, "depth" : 6.35 * mm});
        }
        {
            var Q0;
            {var subQ0=sQuery(id+"F0.wireOp",EDGE,"E5.bottom");var subQ1=sQuery(id+"F0.wireOp",EDGE,"E4");var subQ2=makeQuery(id+"F0.imprint","INTERSECT",VERTEX,{"derivedFrom":[subQ1,subQ0]});Q0=makeQuery(id+"F0.imprint","IMPRINT",FACE,{"disambiguationData":[TD([[makeQuery(id+"F0.imprint","IMPRINT",EDGE,{"disambiguationData":[TD([[subQ2,1.0]])],"derivedFrom":subQ1}),-1.0]])]});}
            extrude(context, id + "F17", {"entities" : qUnion([Q0]), "oppositeDirection" : true, "depth" : 12.7 * mm});
        }
        {
            var Q0;
            {var subQ0=sQuery(id+"F15.wireOp",EDGE,"E49.left");Q0=makeQuery(id+"F15.imprint","IMPRINT",FACE,{"disambiguationData":[TD([[makeQuery(id+"F15.imprint","IMPRINT",EDGE,{"derivedFrom":subQ0}),-1.0]])]});}
            var Q1;
            Q1=sQuery(id+"F15.wireOp",EDGE,"E50");
            revolve(context, id + "F18", {"operationType" : NewBodyOperationType.REMOVE, "entities" : qUnion([Q0]), "axis" : qUnion([Q1]), "revolveType" : RevolveType.FULL, "oppositeDirection" : true});
        }
        {
            var Q0;
            Q0=makeQuery(id+"F4.opExtrude","SWEPT_FACE",FACE,{"disambiguationData":[OSD([sQuery(id+"F0.wireOp",EDGE,"E5.left")])]});
            var sketch = newSketch(context, id + "F19", { "sketchPlane" : qUnion([Q0])});
            skLineSegment(sketch, "E52", {"start": v(251.26, -12.7) * mm, "end": v(251.26, -305.74) * mm});
            skLineSegment(sketch, "E53", {"start": v(-251.26, -12.7) * mm, "end": v(-251.26, -279.4) * mm});
            skLineSegment(sketch, "E54", {"start": v(-251.26, -12.7) * mm, "end": v(251.26, -12.7) * mm});
            skLineSegment(sketch, "E55", {"start": v(-251.26, -279.4) * mm, "end": v(251.26, -305.74) * mm});
            skLineSegment(sketch, "E56", {"start": v(-251.26, -279.4) * mm, "end": v(-251.26, -301.93) * mm});
            skLineSegment(sketch, "E57", {"start": v(-251.26, -301.93) * mm, "end": v(251.26, -328.27) * mm});
            skLineSegment(sketch, "E58", {"start": v(251.26, -328.27) * mm, "end": v(251.26, -305.74) * mm});
            skLineSegment(sketch, "E59", {"start": v(251.26, -305.74) * mm, "end": v(263.95, -306.4) * mm});
            skLineSegment(sketch, "E60", {"start": v(251.26, -328.27) * mm, "end": v(263.95, -328.93) * mm});
            skLineSegment(sketch, "E61", {"start": v(263.95, -328.93) * mm, "end": v(263.95, -306.4) * mm});
            skLineSegment(sketch, "E62", {"start": v(251.26, -305.74) * mm, "end": v(238.58, -305.07) * mm});
            skLineSegment(sketch, "E63", {"start": v(238.58, -305.07) * mm, "end": v(238.58, -327.6) * mm});
            skLineSegment(sketch, "E64", {"start": v(-251.26, -279.4) * mm, "end": v(-263.95, -278.74) * mm});
            skLineSegment(sketch, "E65", {"start": v(-251.26, -301.93) * mm, "end": v(-263.95, -301.27) * mm});
            skLineSegment(sketch, "E66", {"start": v(-263.95, -301.27) * mm, "end": v(-263.95, -278.74) * mm});
            skLineSegment(sketch, "E67", {"start": v(-251.26, -279.4) * mm, "end": v(-238.58, -280.06) * mm});
            skLineSegment(sketch, "E68", {"start": v(-238.58, -280.06) * mm, "end": v(-238.58, -302.6) * mm});
            skSolve(sketch);
        }
        {
            var Q0;
            Q0=makeQuery(id+"F19.imprint","IMPRINT",FACE,{"disambiguationData":[TD([[makeQuery(id+"F19.imprint","IMPRINT",EDGE,{"derivedFrom":sQuery(id+"F19.wireOp",EDGE,"E56")}),-1.0]])]});
            var Q1;
            {var subQ0=sQuery(id+"F19.wireOp",EDGE,"E56");Q1=makeQuery(id+"F19.imprint","IMPRINT",FACE,{"disambiguationData":[TD([[makeQuery(id+"F19.imprint","IMPRINT",EDGE,{"derivedFrom":subQ0}),1.0]])]});}
            var Q2;
            {var subQ0=sQuery(id+"F19.wireOp",EDGE,"E58");Q2=makeQuery(id+"F19.imprint","IMPRINT",FACE,{"disambiguationData":[TD([[makeQuery(id+"F19.imprint","IMPRINT",EDGE,{"derivedFrom":subQ0}),1.0]])]});}
            var Q3;
            Q3=makeQuery(id+"F19.imprint","IMPRINT",FACE,{"disambiguationData":[TD([[makeQuery(id+"F19.imprint","IMPRINT",EDGE,{"derivedFrom":sQuery(id+"F19.wireOp",EDGE,"E58")}),-1.0]])]});
            extrude(context, id + "F20", {"entities" : qUnion([Q0, Q1, Q2, Q3]), "oppositeDirection" : true, "depth" : 914.4 * mm});
        }
        {
            var Q0;
            Q0=makeQuery(id+"F20.opExtrude","CAP_EDGE",EDGE,{"disambiguationData":[OSD([sQuery(id+"F19.wireOp",EDGE,"E61")])],"isStart":false});
            var Q1;
            Q1=makeQuery(id+"F20.opExtrude","CAP_EDGE",EDGE,{"disambiguationData":[OSD([sQuery(id+"F19.wireOp",EDGE,"E63")])],"isStart":false});
            var Q2;
            Q2=makeQuery(id+"F20.opExtrude","CAP_EDGE",EDGE,{"disambiguationData":[OSD([sQuery(id+"F19.wireOp",EDGE,"E68")])],"isStart":false});
            var Q3;
            Q3=makeQuery(id+"F20.opExtrude","CAP_EDGE",EDGE,{"disambiguationData":[OSD([sQuery(id+"F19.wireOp",EDGE,"E66")])],"isStart":false});
            var Q4;
            Q4=makeQuery(id+"F20.opExtrude","CAP_EDGE",EDGE,{"disambiguationData":[OSD([sQuery(id+"F19.wireOp",EDGE,"E61")])],"isStart":true});
            var Q5;
            Q5=makeQuery(id+"F20.opExtrude","CAP_EDGE",EDGE,{"disambiguationData":[OSD([sQuery(id+"F19.wireOp",EDGE,"E63")])],"isStart":true});
            var Q6;
            Q6=makeQuery(id+"F20.opExtrude","CAP_EDGE",EDGE,{"disambiguationData":[OSD([sQuery(id+"F19.wireOp",EDGE,"E66")])],"isStart":true});
            var Q7;
            Q7=makeQuery(id+"F20.opExtrude","CAP_EDGE",EDGE,{"disambiguationData":[OSD([sQuery(id+"F19.wireOp",EDGE,"E68")])],"isStart":true});
            fillet(context, id + "F21", {"entities" : qUnion([Q0, Q1, Q2, Q3, Q4, Q5, Q6, Q7]), "radius" : 12.7 * mm, "tangentPropagation" : true, "allowEdgeOverflow" : false});
        }
    });
